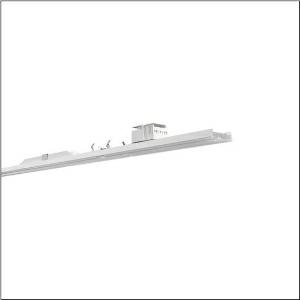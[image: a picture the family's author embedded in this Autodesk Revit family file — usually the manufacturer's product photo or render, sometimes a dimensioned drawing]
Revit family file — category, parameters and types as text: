
# Revit family: licross_r__21_recessed_mo_52tl12dnd75f_9c15
name_source: partatom
category: Lighting Fixtures
units: mm (PartAtom-declared; Revit-internal decimal feet)

## family parameters
Cut with Voids When Loaded = No
Host = Face
Light Source = No
Part Type = Normal
Room Calculation Point = No
Round Connector Dimension = Use Diameter
Shared = No

## types (1)
- --- (1 x LED, 7960 lm, 61.1 W, 4000K)
    Apparent Load = 61 VA
    CIE Flux Codes = 72 92 99 100 100
    Color Rendering = 90
    Color Temperature = 4000K
    Default Elevation = 1800 mm
    Description = Licross® 21 Recessed MO, luminaire insert, of sheet steel, galvanised, coil coated, white, length: 1.500mm, width: 66mm, height: 67mm, LED rated luminous flux: 7.960lm, light colour: 940, control gear: DALI 2, control gear: ECG DALI, with plug, 5-pole, with phase selection, mains connection: 220..240V, AC, 50/60Hz, halogen-free wiring, primary optical cover: cover, of PMMA, light emission: direct distribution, protection rating (complete): IP40, insulation class (complete): insulation class I (protective earthing), certification: CE, ENEC, VDE, UKCA, protection symbol: D if used in an environment without relevant dust loads with corresponding accessories, permissible ambient temperature for indoor applications: -25..+35°C, corresponds to IFS (International Featured Standards) requirements for safety and quality in the food industry, reducing of maximum allowable ambient temperature of 5°C with ceiling mounting, packaging unit: 1 piece
    Height = 58 mm
    Lamp = 1 x LED
    Lamp Light Flux = 7960 lm
    Lamp Power = 61.1 W
    Lamp count = 1
    Length = 1500 mm
    Luminous efficacy = 130 lm/W
    Manufacturer = Siteco
    ModVariant = No
    Model = 52TL12DND75F
    Mounting Place = Ceiling
    Mounting Type = Pendant
    Number of Poles = 1
    OnlyDefault = Yes
    Power Factor = 1
    Product Name = Licross® 21 Recessed MO
    Product group = luminaire insert
    ProductGroupID = 902
    Protection Class = Protection class I
    Protection Degree = IP 40
    RLX_Detail_Level = 1
    RlxData = <blob elided: 22429 chars, md5=86464e47>
    Socket = socket
    Standby Power = 0 W
    System Light Flux = 7960 lm
    System Power = 61 W
    Type Comments = factory setting: luminous flux: 100 % | dim-lin: 254 | 405 mA
    Type Image = l_1266722.jpg
    URL = http://relux.com
    VarID = @adj_128861
    Voltage = 0 V
    Weight = 0.00 kg
    Width = 66 mm

## geometry (parser evidence)
native form markers: Blend x4, Sweep x10
no freeform markers — native parametric forms only
